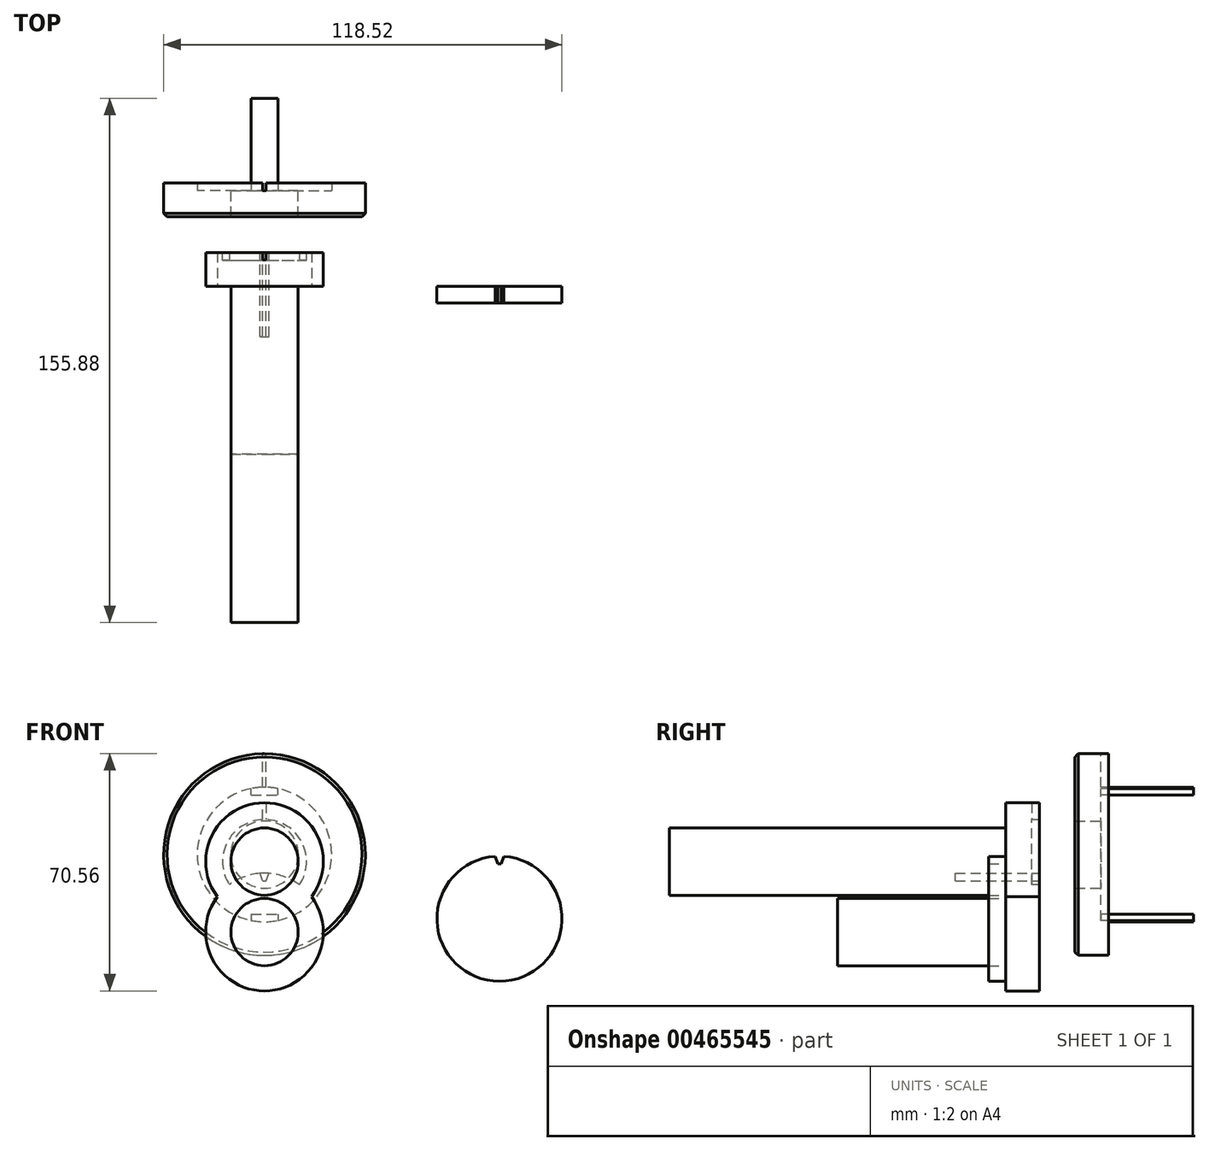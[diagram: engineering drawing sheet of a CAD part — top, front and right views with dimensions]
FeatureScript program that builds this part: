
annotation { "Feature Type Name" : "Feature", "Feature Type Description" : "" }
export const myFeature = defineFeature(function(context is Context, id is Id, definition is map)
    precondition{}
    {
        {
            var Q0;
            Q0=qCreatedBy(makeId("Front.planeOp"),FACE);
            var sketch = newSketch(context, id + "F0", { "sketchPlane" : qUnion([Q0])});
            skCircle(sketch, "E0", {"center": v(0, 0) * mm, "radius": 10 * mm});
            skSolve(sketch);
        }
        {
            var Q0;
            Q0=makeQuery(id+"F0.imprint","IMPRINT",FACE,{"disambiguationData":[TD([[makeQuery(id+"F0.imprint","IMPRINT",EDGE,{"derivedFrom":sQuery(id+"F0.wireOp",EDGE,"E0")}),1.0]])]});
            extrude(context, id + "F1", {"entities" : qUnion([Q0]), "depth" : 50 * mm});
        }
        {
            var Q0;
            Q0=qCreatedBy(makeId("Front.planeOp"),FACE);
            var sketch = newSketch(context, id + "F2", { "sketchPlane" : qUnion([Q0])});
            skCircle(sketch, "E1", {"center": v(0, 20.96) * mm, "radius": 10 * mm});
            skSolve(sketch);
        }
        {
            var Q0;
            Q0=makeQuery(id+"F2.imprint","IMPRINT",FACE,{"disambiguationData":[TD([[makeQuery(id+"F2.imprint","IMPRINT",EDGE,{"derivedFrom":sQuery(id+"F2.wireOp",EDGE,"E1")}),1.0]])]});
            extrude(context, id + "F3", {"entities" : qUnion([Q0]), "depth" : 100 * mm});
        }
        {
            var Q0;
            Q0=qCreatedBy(makeId("Right.planeOp"),FACE);
            var sketch = newSketch(context, id + "F4", { "sketchPlane" : qUnion([Q0])});
            skLineSegment(sketch, "E2", {"start": v(20.63, 53.06) * mm, "end": v(20.63, 23.06) * mm});
            skLineSegment(sketch, "E3", {"start": v(20.63, 53.06) * mm, "end": v(30.63, 53.06) * mm});
            skLineSegment(sketch, "E4", {"start": v(30.63, 53.06) * mm, "end": v(30.63, 43.06) * mm});
            skLineSegment(sketch, "E5", {"start": v(30.63, 43.06) * mm, "end": v(28.38, 43.06) * mm});
            skLineSegment(sketch, "E6", {"start": v(28.38, 43.06) * mm, "end": v(28.38, 23.06) * mm});
            skLineSegment(sketch, "E7", {"start": v(28.38, 23.06) * mm, "end": v(20.63, 23.06) * mm});
            skLineSegment(sketch, "E8", {"start": v(11.12, 23.06) * mm, "end": v(53.98, 23.06) * mm, "construction": true});
            skSolve(sketch);
        }
        {
            var Q0;
            Q0=makeQuery(id+"F4.imprint","IMPRINT",FACE,{"disambiguationData":[TD([[makeQuery(id+"F4.imprint","IMPRINT",EDGE,{"derivedFrom":sQuery(id+"F4.wireOp",EDGE,"E2")}),1.0]])]});
            var Q1;
            Q1=sQuery(id+"F4.wireOp",EDGE,"E8");
            revolve(context, id + "F5", {"entities" : qUnion([Q0]), "axis" : qUnion([Q1]), "revolveType" : RevolveType.FULL});
        }
        {
            var Q0;
            Q0=makeQuery(id+"F5.opRevolve","SWEPT_FACE",FACE,{"disambiguationData":[OSD([sQuery(id+"F4.wireOp",EDGE,"E4")])]});
            var sketch = newSketch(context, id + "F6", { "sketchPlane" : qUnion([Q0])});
            skLineSegment(sketch, "E9", {"start": v(0, 23.06) * mm, "end": v(0, 53.06) * mm, "construction": true});
            skPoint(sketch, "E10", {"position": v(0, 43.06) * mm});
            skLineSegment(sketch, "E11", {"start": v(-0.5, 43.06) * mm, "end": v(-0.5, 53.06) * mm});
            skLineSegment(sketch, "E12", {"start": v(0.5, 43.06) * mm, "end": v(0.5, 53.06) * mm});
            skLineSegment(sketch, "E13", {"start": v(-0.5, 43.06) * mm, "end": v(-0.5, 42.64) * mm});
            skLineSegment(sketch, "E14", {"start": v(-0.5, 42.64) * mm, "end": v(0.5, 42.64) * mm});
            skLineSegment(sketch, "E15", {"start": v(0.5, 42.64) * mm, "end": v(0.5, 43.06) * mm});
            skLineSegment(sketch, "E16", {"start": v(-0.5, 53.06) * mm, "end": v(-0.5, 53.43) * mm});
            skLineSegment(sketch, "E17", {"start": v(-0.5, 53.43) * mm, "end": v(0.5, 53.43) * mm});
            skLineSegment(sketch, "E18", {"start": v(0.5, 53.43) * mm, "end": v(0.5, 53.06) * mm});
            skSolve(sketch);
        }
        {
            var Q0;
            Q0 = qSketchRegion(id + "F6", true);
            extrude(context, id + "F7", {"entities" : qUnion([Q0]), "operationType" : NewBodyOperationType.REMOVE, "oppositeDirection" : true, "depth" : 2.24 * mm});
        }
        {
            var Q0;
            Q0=makeQuery(id+"F5.opRevolve","SWEPT_EDGE",EDGE,{"disambiguationData":[OSD([sQuery(id+"F4.wireOp",EDGE,"E2"),sQuery(id+"F4.wireOp",EDGE,"E3")])]});
            chamfer(context, id + "F8", {"entities" : qUnion([Q0]), "width" : 1 * mm, "tangentPropagation" : true});
        }
        {
            var Q0;
            Q0=makeQuery(id+"F5.opRevolve","SWEPT_FACE",FACE,{"disambiguationData":[OSD([sQuery(id+"F4.wireOp",EDGE,"E6")])]});
            var sketch = newSketch(context, id + "F9", { "sketchPlane" : qUnion([Q0])});
            skCircle(sketch, "E19", {"center": v(0, 23.06) * mm, "radius": 10 * mm});
            skSolve(sketch);
        }
        {
            var Q0;
            Q0=makeQuery(id+"F9.imprint","IMPRINT",FACE,{"disambiguationData":[TD([[makeQuery(id+"F9.imprint","IMPRINT",EDGE,{"derivedFrom":sQuery(id+"F9.wireOp",EDGE,"E19")}),1.0]])]});
            extrude(context, id + "F10", {"entities" : qUnion([Q0]), "operationType" : NewBodyOperationType.REMOVE, "oppositeDirection" : true, "depth" : 15 * mm});
        }
        {
            var Q0;
            Q0=makeQuery(id+"F3.opExtrude","CAP_FACE",FACE,{"disambiguationData":[OSD([sQuery(id+"F2.wireOp",EDGE,"E1")])],"isStart":true});
            var sketch = newSketch(context, id + "F11", { "sketchPlane" : qUnion([Q0])});
            skCircle(sketch, "E20", {"center": v(0, 20.96) * mm, "radius": 17.5 * mm});
            skSolve(sketch);
        }
        {
            var Q0;
            Q0=makeQuery(id+"F11.imprint","IMPRINT",FACE,{"disambiguationData":[TD([[makeQuery(id+"F11.imprint","IMPRINT",EDGE,{"derivedFrom":makeQuery(id+"F3.opExtrude","CAP_EDGE",EDGE,{"disambiguationData":[OSD([sQuery(id+"F2.wireOp",EDGE,"E1")])],"isStart":true})}),-1.0]])]});
            var Q1;
            Q1=makeQuery(id+"F11.imprint","IMPRINT",FACE,{"disambiguationData":[TD([[makeQuery(id+"F11.imprint","IMPRINT",EDGE,{"derivedFrom":sQuery(id+"F11.wireOp",EDGE,"E20")}),1.0]])]});
            extrude(context, id + "F12", {"entities" : qUnion([Q0, Q1]), "operationType" : NewBodyOperationType.ADD, "depth" : 10 * mm});
        }
        {
            var Q0;
            Q0=makeQuery(id+"F12.opExtrude","CAP_FACE",FACE,{"disambiguationData":[OSD([sQuery(id+"F11.wireOp",EDGE,"E20")])],"isStart":false});
            var sketch = newSketch(context, id + "F13", { "sketchPlane" : qUnion([Q0])});
            skCircle(sketch, "E21", {"center": v(0, 20.96) * mm, "radius": 12.5 * mm});
            skSolve(sketch);
        }
        {
            var Q0;
            Q0=makeQuery(id+"F13.imprint","IMPRINT",FACE,{"disambiguationData":[TD([[makeQuery(id+"F13.imprint","IMPRINT",EDGE,{"derivedFrom":sQuery(id+"F13.wireOp",EDGE,"E21")}),1.0]])]});
            extrude(context, id + "F14", {"entities" : qUnion([Q0]), "operationType" : NewBodyOperationType.REMOVE, "oppositeDirection" : true, "depth" : 2.25 * mm});
        }
        {
            var Q0;
            Q0=makeQuery(id+"F12.opExtrude","CAP_FACE",FACE,{"disambiguationData":[OSD([sQuery(id+"F11.wireOp",EDGE,"E20")])],"isStart":false});
            var sketch = newSketch(context, id + "F15", { "sketchPlane" : qUnion([Q0])});
            skLineSegment(sketch, "E22", {"start": v(0, 20.96) * mm, "end": v(0, 38.46) * mm, "construction": true});
            skPoint(sketch, "E23", {"position": v(0, 33.46) * mm});
            skLineSegment(sketch, "E24", {"start": v(0, 33.46) * mm, "end": v(0.5, 33.45) * mm});
            skLineSegment(sketch, "E25", {"start": v(0, 33.46) * mm, "end": v(-0.5, 33.45) * mm});
            skLineSegment(sketch, "E26", {"start": v(0, 38.46) * mm, "end": v(-0.5, 38.46) * mm});
            skLineSegment(sketch, "E27", {"start": v(0, 38.46) * mm, "end": v(0.5, 38.46) * mm});
            skLineSegment(sketch, "E28", {"start": v(-0.5, 38.46) * mm, "end": v(-0.5, 33.45) * mm});
            skLineSegment(sketch, "E29", {"start": v(0.5, 33.45) * mm, "end": v(0.5, 38.46) * mm});
            skSolve(sketch);
        }
        {
            var Q0;
            {var subQ6=makeQuery(id+"F12.opExtrude","CAP_EDGE",EDGE,{"disambiguationData":[OSD([sQuery(id+"F11.wireOp",EDGE,"E20")])],"isStart":false});var subQ8=sQuery(id+"F15.wireOp",EDGE,"E28");var subQ10=makeQuery(id+"F15.imprint","INTERSECT",VERTEX,{"derivedFrom":[subQ6,subQ8]});Q0=makeQuery(id+"F15.imprint","IMPRINT",FACE,{"disambiguationData":[TD([[makeQuery(id+"F15.imprint","IMPRINT",EDGE,{"disambiguationData":[TD([[subQ10,-1.0]])],"derivedFrom":subQ8}),1.0]])]});}
            extrude(context, id + "F16", {"entities" : qUnion([Q0]), "operationType" : NewBodyOperationType.REMOVE, "oppositeDirection" : true, "depth" : 2.24 * mm});
        }
        {
            var Q0;
            Q0=makeQuery(id+"F5.opRevolve","SWEPT_FACE",FACE,{"disambiguationData":[OSD([sQuery(id+"F4.wireOp",EDGE,"E6")])]});
            var sketch = newSketch(context, id + "F17", { "sketchPlane" : qUnion([Q0])});
            skLineSegment(sketch, "E30", {"start": v(0, 23.06) * mm, "end": v(0, 43.06) * mm, "construction": true});
            skLineSegment(sketch, "E31", {"start": v(0, 23.06) * mm, "end": v(0, 3.06) * mm, "construction": true});
            skLineSegment(sketch, "E32", {"start": v(0, 3.06) * mm, "end": v(0, 5.36) * mm, "construction": true});
            skLineSegment(sketch, "E33", {"start": v(0, 5.36) * mm, "end": v(-3.98, 5.36) * mm});
            skLineSegment(sketch, "E34", {"start": v(-3.98, 5.36) * mm, "end": v(-3.98, 3.46) * mm});
            skLineSegment(sketch, "E35", {"start": v(0, 5.36) * mm, "end": v(3.98, 5.36) * mm});
            skLineSegment(sketch, "E36", {"start": v(3.98, 5.36) * mm, "end": v(3.98, 3.46) * mm});
            skLineSegment(sketch, "E37", {"start": v(0, 43.06) * mm, "end": v(0, 40.76) * mm, "construction": true});
            skLineSegment(sketch, "E38", {"start": v(0, 40.76) * mm, "end": v(-3.98, 40.76) * mm});
            skLineSegment(sketch, "E39", {"start": v(-3.98, 40.76) * mm, "end": v(-3.98, 42.66) * mm});
            skLineSegment(sketch, "E40", {"start": v(0, 40.76) * mm, "end": v(3.98, 40.76) * mm});
            skLineSegment(sketch, "E41", {"start": v(3.98, 40.76) * mm, "end": v(3.98, 42.66) * mm});
            skSolve(sketch);
        }
        {
            var Q0;
            Q0=makeQuery(id+"F17.imprint","IMPRINT",FACE,{"disambiguationData":[TD([[makeQuery(id+"F17.imprint","IMPRINT",EDGE,{"derivedFrom":sQuery(id+"F17.wireOp",EDGE,"E33")}),1.0]])]});
            var Q1;
            Q1=makeQuery(id+"F17.imprint","IMPRINT",FACE,{"disambiguationData":[TD([[makeQuery(id+"F17.imprint","IMPRINT",EDGE,{"derivedFrom":sQuery(id+"F17.wireOp",EDGE,"E38")}),-1.0]])]});
            extrude(context, id + "F18", {"entities" : qUnion([Q0, Q1]), "operationType" : NewBodyOperationType.ADD, "depth" : 27.5 * mm});
        }
        {
            var Q0;
            Q0=qCreatedBy(makeId("Front.planeOp"),FACE);
            var sketch = newSketch(context, id + "F19", { "sketchPlane" : qUnion([Q0])});
            skCircle(sketch, "E42", {"center": v(69.92, 3.95) * mm, "radius": 18.6 * mm});
            skSolve(sketch);
        }
        {
            var Q0;
            Q0=makeQuery(id+"F19.imprint","IMPRINT",FACE,{"disambiguationData":[TD([[makeQuery(id+"F19.imprint","IMPRINT",EDGE,{"derivedFrom":sQuery(id+"F19.wireOp",EDGE,"E42")}),1.0]])]});
            extrude(context, id + "F20", {"entities" : qUnion([Q0]), "depth" : 5 * mm});
        }
        {
            var Q0;
            Q0=makeQuery(id+"F20.opExtrude","CAP_FACE",FACE,{"disambiguationData":[OSD([sQuery(id+"F19.wireOp",EDGE,"E42")])],"isStart":true});
            var sketch = newSketch(context, id + "F21", { "sketchPlane" : qUnion([Q0])});
            skLineSegment(sketch, "E43", {"start": v(-69.92, 3.95) * mm, "end": v(-69.92, 22.55) * mm, "construction": true});
            skLineSegment(sketch, "E44", {"start": v(-69.92, 22.55) * mm, "end": v(-69.92, 20.3) * mm, "construction": true});
            skLineSegment(sketch, "E45", {"start": v(-69.92, 20.3) * mm, "end": v(-70.42, 20.3) * mm});
            skLineSegment(sketch, "E46", {"start": v(-69.92, 20.3) * mm, "end": v(-69.42, 20.3) * mm});
            skLineSegment(sketch, "E47", {"start": v(-69.42, 20.3) * mm, "end": v(-68.62, 22.5) * mm});
            skLineSegment(sketch, "E48", {"start": v(-70.42, 20.3) * mm, "end": v(-71.22, 22.5) * mm});
            skSolve(sketch);
        }
        {
            var Q0;
            Q0=makeQuery(id+"F21.imprint","IMPRINT",FACE,{"disambiguationData":[TD([[makeQuery(id+"F21.imprint","IMPRINT",EDGE,{"derivedFrom":sQuery(id+"F21.wireOp",EDGE,"E45")}),-1.0]])]});
            extrude(context, id + "F22", {"entities" : qUnion([Q0]), "operationType" : NewBodyOperationType.REMOVE, "oppositeDirection" : true, "depth" : 25 * mm});
        }
        {
            var Q0;
            Q0=makeQuery(id+"F1.opExtrude","CAP_FACE",FACE,{"disambiguationData":[OSD([sQuery(id+"F0.wireOp",EDGE,"E0")])],"isStart":true});
            var sketch = newSketch(context, id + "F23", { "sketchPlane" : qUnion([Q0])});
            skCircle(sketch, "E49", {"center": v(0, 0) * mm, "radius": 17.5 * mm});
            skSolve(sketch);
        }
        {
            var Q0;
            Q0=makeQuery(id+"F23.imprint","IMPRINT",FACE,{"disambiguationData":[TD([[makeQuery(id+"F23.imprint","IMPRINT",EDGE,{"derivedFrom":makeQuery(id+"F1.opExtrude","CAP_EDGE",EDGE,{"disambiguationData":[OSD([sQuery(id+"F0.wireOp",EDGE,"E0")])],"isStart":true})}),-1.0]])]});
            var Q1;
            Q1=makeQuery(id+"F23.imprint","IMPRINT",FACE,{"disambiguationData":[TD([[makeQuery(id+"F23.imprint","IMPRINT",EDGE,{"derivedFrom":sQuery(id+"F23.wireOp",EDGE,"E49")}),1.0]])]});
            extrude(context, id + "F24", {"entities" : qUnion([Q0, Q1]), "operationType" : NewBodyOperationType.ADD, "depth" : 10 * mm});
        }
        {
            var Q0;
            Q0=makeQuery(id+"F24.opExtrude","CAP_FACE",FACE,{"disambiguationData":[OSD([sQuery(id+"F23.wireOp",EDGE,"E49")])],"isStart":false});
            var sketch = newSketch(context, id + "F25", { "sketchPlane" : qUnion([Q0])});
            skLineSegment(sketch, "E50", {"start": v(0, 0) * mm, "end": v(0, 17.5) * mm, "construction": true});
            skLineSegment(sketch, "E51", {"start": v(0, 17.5) * mm, "end": v(0, 15.25) * mm, "construction": true});
            skLineSegment(sketch, "E52", {"start": v(0, 15.25) * mm, "end": v(0.5, 15.25) * mm});
            skLineSegment(sketch, "E53", {"start": v(0, 15.25) * mm, "end": v(-0.5, 15.25) * mm});
            skLineSegment(sketch, "E54", {"start": v(-0.5, 15.25) * mm, "end": v(-1.3, 17.45) * mm});
            skLineSegment(sketch, "E55", {"start": v(0.5, 15.25) * mm, "end": v(1.3, 17.45) * mm});
            skSolve(sketch);
        }
        {
            var Q0;
            Q0=makeQuery(id+"F25.imprint","IMPRINT",FACE,{"disambiguationData":[TD([[makeQuery(id+"F25.imprint","IMPRINT",EDGE,{"derivedFrom":sQuery(id+"F25.wireOp",EDGE,"E52")}),1.0]])]});
            extrude(context, id + "F26", {"entities" : qUnion([Q0]), "operationType" : NewBodyOperationType.REMOVE, "oppositeDirection" : true, "depth" : 25 * mm});
        }
    });
